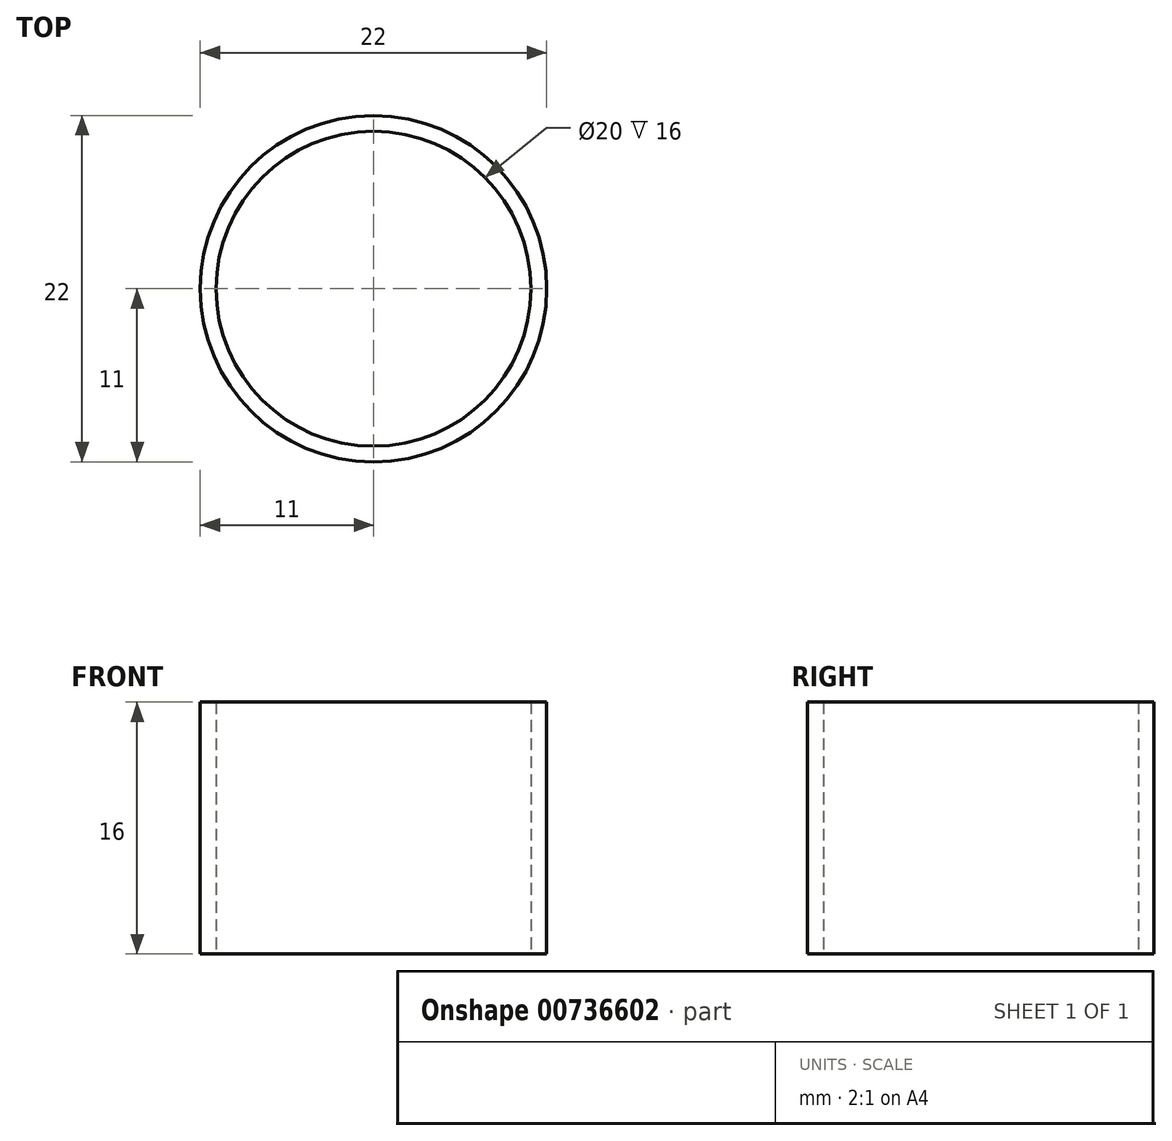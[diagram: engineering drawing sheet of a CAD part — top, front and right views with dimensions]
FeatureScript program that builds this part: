
annotation { "Feature Type Name" : "Feature", "Feature Type Description" : "" }
export const myFeature = defineFeature(function(context is Context, id is Id, definition is map)
    precondition{}
    {
        {
            var Q0;
            Q0=qCreatedBy(makeId("Top.planeOp"),FACE);
            var sketch = newSketch(context, id + "F0", { "sketchPlane" : qUnion([Q0])});
            skCircle(sketch, "E0", {"center": v(0, 0) * mm, "radius": 10 * mm});
            skCircle(sketch, "E1", {"center": v(0, 0) * mm, "radius": 11 * mm});
            skSolve(sketch);
        }
        {
            var Q0;
            Q0 = qSketchRegion(id + "F0", true);
            extrude(context, id + "F1", {"entities" : qUnion([Q0]), "depth" : 16 * mm, "offsetDistance" : 25 * mm});
        }
    });
